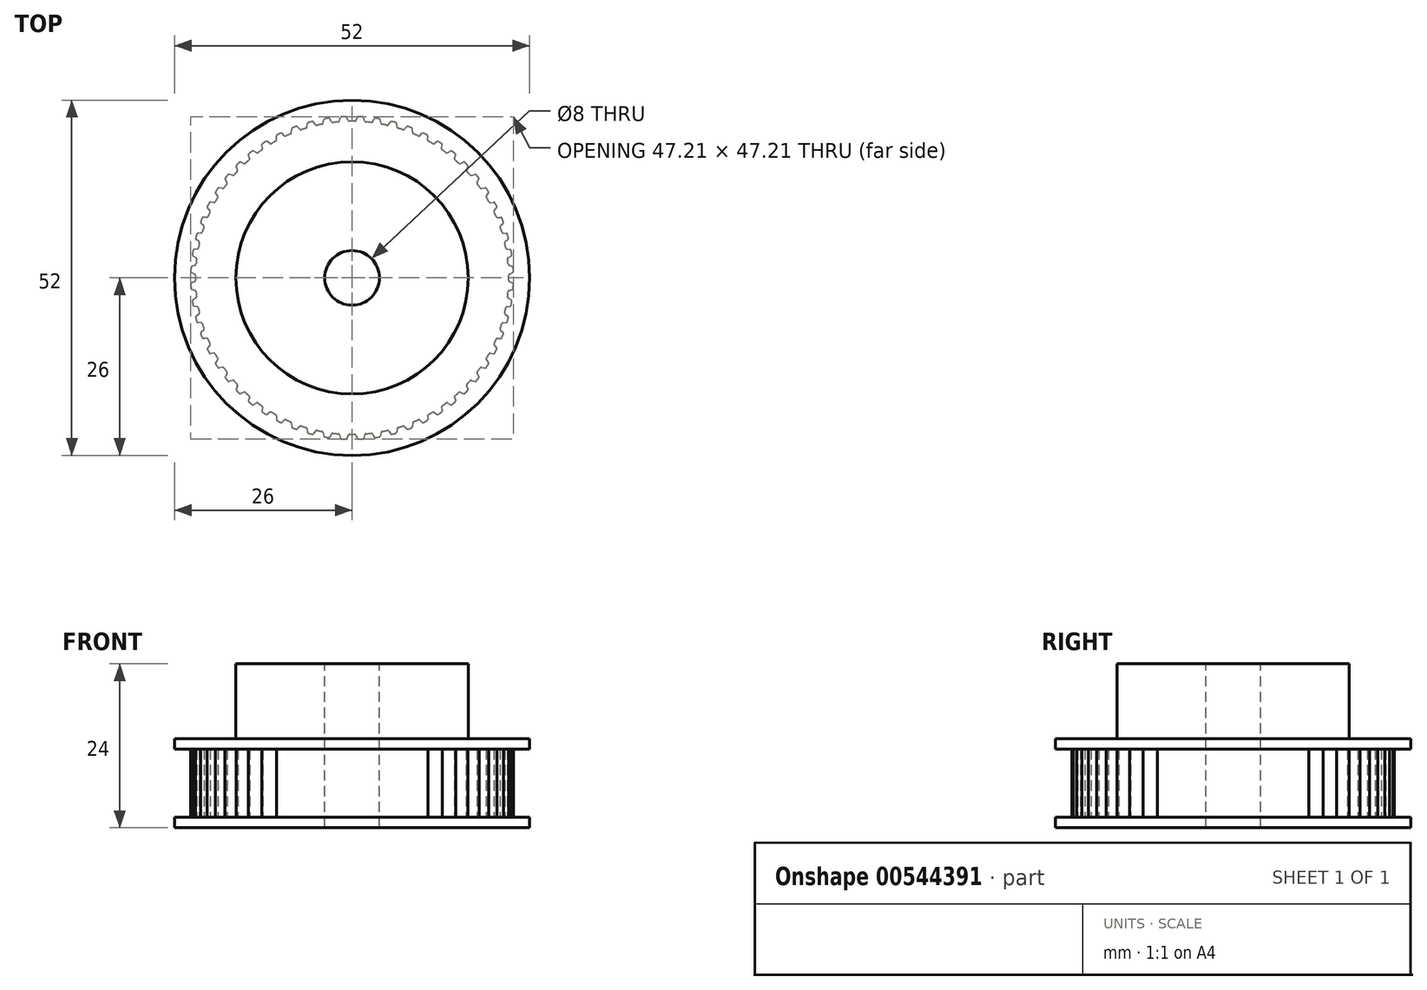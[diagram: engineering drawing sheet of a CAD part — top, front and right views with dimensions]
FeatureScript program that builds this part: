
annotation { "Feature Type Name" : "Feature", "Feature Type Description" : "" }
export const myFeature = defineFeature(function(context is Context, id is Id, definition is map)
    precondition{}
    {
        {
            assignVariable(context, id + "F0", {"name" : "teeth", "anyValue" : 60});
        }
        {
            assignVariable(context, id + "F1", {"name" : "width", "anyValue" : 10});
        }
        {
            var Q0;
            Q0=qCreatedBy(makeId("Top.planeOp"),FACE);
            var sketch = newSketch(context, id + "F2", { "sketchPlane" : qUnion([Q0])});
            skLineSegment(sketch, "E0", {"start": v(0, 0) * mm, "end": v(0, 24.25) * mm, "construction": true});
            skArc(sketch, "E1", {"start": v(1.96, 23.54) * mm, "mid": v(0, 23.62) * mm, "end": v(-1.96, 23.54) * mm, "construction": true});
            skArc(sketch, "E2", {"start": v(1.25, 23.84) * mm, "mid": v(0, 23.87) * mm, "end": v(-1.25, 23.84) * mm, "construction": true});
            skLineSegment(sketch, "E3", {"start": v(1.24, 23.6) * mm, "end": v(0, 0) * mm});
            skLineSegment(sketch, "E4", {"start": v(0, 0) * mm, "end": v(-1.24, 23.6) * mm});
            skArc(sketch, "E5", {"start": v(0.5, 22.92) * mm, "mid": v(0, 22.92) * mm, "end": v(-0.5, 22.92) * mm, "construction": true});
            skArc(sketch, "E6", {"start": v(-0.37, 22.92) * mm, "mid": v(0, 22.92) * mm, "end": v(0.37, 22.92) * mm});
            skLineSegment(sketch, "E7", {"start": v(-0.55, 23.04) * mm, "end": v(-0.77, 23.49) * mm});
            skLineSegment(sketch, "E8", {"start": v(0.55, 23.04) * mm, "end": v(0.77, 23.49) * mm});
            skArc(sketch, "E9", {"start": v(-1.24, 23.6) * mm, "mid": v(-1.1, 23.6) * mm, "end": v(-0.96, 23.6) * mm});
            skArc(sketch, "E10", {"start": v(0.96, 23.6) * mm, "mid": v(1.1, 23.6) * mm, "end": v(1.24, 23.6) * mm});
            skPoint(sketch, "E11.visualSharp", {"position": v(-0.5, 22.92) * mm});
            skArc(sketch, "E11.filletArc", {"start": v(-0.55, 23.04) * mm, "mid": v(-0.48, 22.95) * mm, "end": v(-0.37, 22.92) * mm});
            skPoint(sketch, "E12.visualSharp", {"position": v(0.5, 22.92) * mm});
            skArc(sketch, "E12.filletArc", {"start": v(0.37, 22.92) * mm, "mid": v(0.48, 22.95) * mm, "end": v(0.55, 23.04) * mm});
            skPoint(sketch, "E13.visualSharp", {"position": v(-0.82, 23.6) * mm});
            skArc(sketch, "E13.filletArc", {"start": v(-0.77, 23.49) * mm, "mid": v(-0.84, 23.57) * mm, "end": v(-0.96, 23.6) * mm});
            skPoint(sketch, "E14.visualSharp", {"position": v(0.82, 23.6) * mm});
            skArc(sketch, "E14.filletArc", {"start": v(0.96, 23.6) * mm, "mid": v(0.84, 23.57) * mm, "end": v(0.77, 23.49) * mm});
            skSolve(sketch);
        }
        {
            var Q0;
            Q0=makeQuery(id+"F2.imprint","IMPRINT",FACE,{"disambiguationData":[TD([[makeQuery(id+"F2.imprint","IMPRINT",EDGE,{"derivedFrom":sQuery(id+"F2.wireOp",EDGE,"P1uhFWbC-AUpd-SlUc-z3bf-78FxmXMfxVC7")}),-1.0]])]});
            var Q1;
            {var subQ1=sQuery(id+"F2.wireOp",EDGE,"N9a9pOVT-NxnP-9PMo-Yz0L-ytRW1WlfzG62");Q1=makeQuery(id+"F2.imprint","IMPRINT",FACE,{"disambiguationData":[TD([[makeQuery(id+"F2.imprint","IMPRINT",EDGE,{"derivedFrom":subQ1}),-1.0]])]});}
            var Q2;
            {var subQ0=sQuery(id+"F2.wireOp",EDGE,"E3");Q2=makeQuery(id+"F2.imprint","IMPRINT",FACE,{"disambiguationData":[TD([[makeQuery(id+"F2.imprint","IMPRINT",EDGE,{"derivedFrom":subQ0}),-1.0]])]});}
            extrude(context, id + "F3", {"entities" : qUnion([Q0, Q1, Q2]), "depth" : (getVariable(context, 'width')) * mm, "offsetDistance" : 25 * mm, "symmetric" : true});
        }
        {
            var Q0;
            Q0=makeQuery(id+"F3.opExtrude","SWEPT_BODY",BODY,{"disambiguationData":[OSD([sQuery(id+"F2.wireOp",EDGE,"E1"),sQuery(id+"F2.wireOp",EDGE,"P1uhFWbC-AUpd-SlUc-z3bf-78FxmXMfxVC7"),sQuery(id+"F2.wireOp",EDGE,"WtW3y5By-gfdo-wMA2-XeKf-OYMCoWhlFWBV"),sQuery(id+"F2.wireOp",EDGE,"E3"),sQuery(id+"F2.wireOp",EDGE,"E4"),sQuery(id+"F2.wireOp",EDGE,"N9a9pOVT-NxnP-9PMo-Yz0L-ytRW1WlfzG62"),sQuery(id+"F2.wireOp",EDGE,"aZysBSW6-xeYk-Y5AL-URpO-NHl3PhOeUQth"),sQuery(id+"F2.wireOp",EDGE,"Rlz8ElYD-njMK-K2Gw-WVJm-wIMkdtHgt6w2"),sQuery(id+"F2.wireOp",EDGE,"dd8ef0db-efd4-4436-b532-5508418b62120.MirrorCS"),sQuery(id+"F2.wireOp",EDGE,"e644996f-e673-4261-af5f-634a3a17fb890.MirrorCS"),sQuery(id+"F2.wireOp",EDGE,"3e81cde9-3123-4241-844a-bf780b0a6bc10.MirrorCS")])]});
            var Q1;
            Q1=makeQuery(id+"F3.opExtrude","SWEPT_EDGE",EDGE,{"disambiguationData":[OSD([sQuery(id+"F2.wireOp",EDGE,"E3"),sQuery(id+"F2.wireOp",EDGE,"E4")])]});
            circularPattern(context, id + "F4", {"operationType" : NewBodyOperationType.ADD, "entities" : qUnion([Q0]), "axis" : qUnion([Q1]), "angle" : 360 * degree, "instanceCount" : getVariable(context, 'teeth'), "equalSpace" : true});
        }
        {
            var Q0;
            {var subQ0=makeQuery(id+"F3.opExtrude","CAP_FACE",FACE,{"disambiguationData":[OSD([sQuery(id+"F2.wireOp",EDGE,"E3"),sQuery(id+"F2.wireOp",EDGE,"E4"),sQuery(id+"F2.wireOp",EDGE,"E6"),sQuery(id+"F2.wireOp",EDGE,"E7"),sQuery(id+"F2.wireOp",EDGE,"E8"),sQuery(id+"F2.wireOp",EDGE,"E9"),sQuery(id+"F2.wireOp",EDGE,"E10"),sQuery(id+"F2.wireOp",EDGE,"E11.filletArc"),sQuery(id+"F2.wireOp",EDGE,"E12.filletArc"),sQuery(id+"F2.wireOp",EDGE,"E13.filletArc"),sQuery(id+"F2.wireOp",EDGE,"E14.filletArc")])],"isStart":false});Q0=makeQuery(id+"F4.boolean.opBoolean","MERGE",FACE,{"derivedFrom":[subQ0,makeQuery(id+"F4.opPattern","COPY",FACE,{"derivedFrom":subQ0,"instanceName":"1"}),makeQuery(id+"F4.opPattern","COPY",FACE,{"derivedFrom":subQ0,"instanceName":"2"}),makeQuery(id+"F4.opPattern","COPY",FACE,{"derivedFrom":subQ0,"instanceName":"3"}),makeQuery(id+"F4.opPattern","COPY",FACE,{"derivedFrom":subQ0,"instanceName":"4"}),makeQuery(id+"F4.opPattern","COPY",FACE,{"derivedFrom":subQ0,"instanceName":"5"}),makeQuery(id+"F4.opPattern","COPY",FACE,{"derivedFrom":subQ0,"instanceName":"6"}),makeQuery(id+"F4.opPattern","COPY",FACE,{"derivedFrom":subQ0,"instanceName":"7"}),makeQuery(id+"F4.opPattern","COPY",FACE,{"derivedFrom":subQ0,"instanceName":"8"}),makeQuery(id+"F4.opPattern","COPY",FACE,{"derivedFrom":subQ0,"instanceName":"9"}),makeQuery(id+"F4.opPattern","COPY",FACE,{"derivedFrom":subQ0,"instanceName":"10"}),makeQuery(id+"F4.opPattern","COPY",FACE,{"derivedFrom":subQ0,"instanceName":"11"}),makeQuery(id+"F4.opPattern","COPY",FACE,{"derivedFrom":subQ0,"instanceName":"12"}),makeQuery(id+"F4.opPattern","COPY",FACE,{"derivedFrom":subQ0,"instanceName":"13"}),makeQuery(id+"F4.opPattern","COPY",FACE,{"derivedFrom":subQ0,"instanceName":"14"}),makeQuery(id+"F4.opPattern","COPY",FACE,{"derivedFrom":subQ0,"instanceName":"15"}),makeQuery(id+"F4.opPattern","COPY",FACE,{"derivedFrom":subQ0,"instanceName":"16"}),makeQuery(id+"F4.opPattern","COPY",FACE,{"derivedFrom":subQ0,"instanceName":"17"})]});}
            var sketch = newSketch(context, id + "F5", { "sketchPlane" : qUnion([Q0])});
            skCircle(sketch, "E15", {"center": v(0, 0) * mm, "radius": 26 * mm});
            skSolve(sketch);
        }
        {
            var Q0;
            Q0=qSketchRegion(id+"F5",true);
            extrude(context, id + "F6", {"entities" : qUnion([Q0]), "operationType" : NewBodyOperationType.ADD, "depth" : 1.5 * mm, "offsetDistance" : 25 * mm});
        }
        {
            var Q0;
            {var subQ0=makeQuery(id+"F3.opExtrude","CAP_FACE",FACE,{"disambiguationData":[OSD([sQuery(id+"F2.wireOp",EDGE,"E3"),sQuery(id+"F2.wireOp",EDGE,"E4"),sQuery(id+"F2.wireOp",EDGE,"E6"),sQuery(id+"F2.wireOp",EDGE,"E7"),sQuery(id+"F2.wireOp",EDGE,"E8"),sQuery(id+"F2.wireOp",EDGE,"E9"),sQuery(id+"F2.wireOp",EDGE,"E10"),sQuery(id+"F2.wireOp",EDGE,"E11.filletArc"),sQuery(id+"F2.wireOp",EDGE,"E12.filletArc"),sQuery(id+"F2.wireOp",EDGE,"E13.filletArc"),sQuery(id+"F2.wireOp",EDGE,"E14.filletArc")])],"isStart":true});Q0=makeQuery(id+"F4.boolean.opBoolean","MERGE",FACE,{"derivedFrom":[subQ0,makeQuery(id+"F4.opPattern","COPY",FACE,{"derivedFrom":subQ0,"instanceName":"1"}),makeQuery(id+"F4.opPattern","COPY",FACE,{"derivedFrom":subQ0,"instanceName":"2"}),makeQuery(id+"F4.opPattern","COPY",FACE,{"derivedFrom":subQ0,"instanceName":"3"}),makeQuery(id+"F4.opPattern","COPY",FACE,{"derivedFrom":subQ0,"instanceName":"4"}),makeQuery(id+"F4.opPattern","COPY",FACE,{"derivedFrom":subQ0,"instanceName":"5"}),makeQuery(id+"F4.opPattern","COPY",FACE,{"derivedFrom":subQ0,"instanceName":"6"}),makeQuery(id+"F4.opPattern","COPY",FACE,{"derivedFrom":subQ0,"instanceName":"7"}),makeQuery(id+"F4.opPattern","COPY",FACE,{"derivedFrom":subQ0,"instanceName":"8"}),makeQuery(id+"F4.opPattern","COPY",FACE,{"derivedFrom":subQ0,"instanceName":"9"}),makeQuery(id+"F4.opPattern","COPY",FACE,{"derivedFrom":subQ0,"instanceName":"10"}),makeQuery(id+"F4.opPattern","COPY",FACE,{"derivedFrom":subQ0,"instanceName":"11"}),makeQuery(id+"F4.opPattern","COPY",FACE,{"derivedFrom":subQ0,"instanceName":"12"}),makeQuery(id+"F4.opPattern","COPY",FACE,{"derivedFrom":subQ0,"instanceName":"13"}),makeQuery(id+"F4.opPattern","COPY",FACE,{"derivedFrom":subQ0,"instanceName":"14"}),makeQuery(id+"F4.opPattern","COPY",FACE,{"derivedFrom":subQ0,"instanceName":"15"}),makeQuery(id+"F4.opPattern","COPY",FACE,{"derivedFrom":subQ0,"instanceName":"16"}),makeQuery(id+"F4.opPattern","COPY",FACE,{"derivedFrom":subQ0,"instanceName":"17"}),makeQuery(id+"F4.opPattern","COPY",FACE,{"derivedFrom":subQ0,"instanceName":"18"}),makeQuery(id+"F4.opPattern","COPY",FACE,{"derivedFrom":subQ0,"instanceName":"19"}),makeQuery(id+"F4.opPattern","COPY",FACE,{"derivedFrom":subQ0,"instanceName":"20"}),makeQuery(id+"F4.opPattern","COPY",FACE,{"derivedFrom":subQ0,"instanceName":"21"}),makeQuery(id+"F4.opPattern","COPY",FACE,{"derivedFrom":subQ0,"instanceName":"22"}),makeQuery(id+"F4.opPattern","COPY",FACE,{"derivedFrom":subQ0,"instanceName":"23"}),makeQuery(id+"F4.opPattern","COPY",FACE,{"derivedFrom":subQ0,"instanceName":"24"}),makeQuery(id+"F4.opPattern","COPY",FACE,{"derivedFrom":subQ0,"instanceName":"25"}),makeQuery(id+"F4.opPattern","COPY",FACE,{"derivedFrom":subQ0,"instanceName":"26"}),makeQuery(id+"F4.opPattern","COPY",FACE,{"derivedFrom":subQ0,"instanceName":"27"}),makeQuery(id+"F4.opPattern","COPY",FACE,{"derivedFrom":subQ0,"instanceName":"28"}),makeQuery(id+"F4.opPattern","COPY",FACE,{"derivedFrom":subQ0,"instanceName":"29"})]});}
            var sketch = newSketch(context, id + "F7", { "sketchPlane" : qUnion([Q0])});
            skCircle(sketch, "E16", {"center": v(0, 0) * mm, "radius": 26 * mm});
            skSolve(sketch);
        }
        {
            var Q0;
            Q0=qSketchRegion(id+"F7",true);
            extrude(context, id + "F8", {"entities" : qUnion([Q0]), "operationType" : NewBodyOperationType.ADD, "depth" : 1.5 * mm, "offsetDistance" : 25 * mm});
        }
        {
            var Q0;
            Q0=makeQuery(id+"F6.opExtrude","CAP_FACE",FACE,{"disambiguationData":[OSD([sQuery(id+"F5.wireOp",EDGE,"E15")])],"isStart":false});
            var sketch = newSketch(context, id + "F9", { "sketchPlane" : qUnion([Q0])});
            skCircle(sketch, "E17", {"center": v(0, 0) * mm, "radius": 17 * mm});
            skSolve(sketch);
        }
        {
            var Q0;
            Q0=qSketchRegion(id+"F9",true);
            extrude(context, id + "F10", {"entities" : qUnion([Q0]), "operationType" : NewBodyOperationType.ADD, "depth" : 11 * mm, "offsetDistance" : 25 * mm});
        }
        {
            var Q0;
            Q0=makeQuery(id+"F10.opExtrude","CAP_FACE",FACE,{"disambiguationData":[OSD([sQuery(id+"F9.wireOp",EDGE,"E17")])],"isStart":false});
            var sketch = newSketch(context, id + "F11", { "sketchPlane" : qUnion([Q0])});
            skCircle(sketch, "E18", {"center": v(0, 0) * mm, "radius": 4 * mm});
            skSolve(sketch);
        }
        {
            var Q0;
            Q0=qSketchRegion(id+"F11",true);
            extrude(context, id + "F12", {"entities" : qUnion([Q0]), "operationType" : NewBodyOperationType.REMOVE, "endBound" : BoundingType.THROUGH_ALL, "oppositeDirection" : true, "depth" : 25 * mm, "offsetDistance" : 25 * mm});
        }
    });
